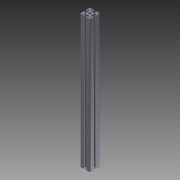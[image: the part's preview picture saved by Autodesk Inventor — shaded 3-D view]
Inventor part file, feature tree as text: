
AUTODESK INVENTOR PART (.ipt)
format: ipt  version: 2016 (Build 200138000, 138)  size: 215,552 bytes
history: native  units: mm
features: other x42, sketch x5, hole x4, extrude x1
ambient origin geometry x8: Origin, YZ Plane, XZ Plane, XY Plane, X Axis, Y Axis, Z Axis, Center Point
bodies: Solid1 (feature_tree)
feature tree (52):
  extrude  "Extrusion1"  [1 undecoded]
  hole  "Drilling 1"  [1 undecoded]
  hole  "Drilling 2"  [1 undecoded]
  hole  "Drilling 3"  [1 undecoded]
  hole  "Drilling 4"  [1 undecoded]
  other  "side_4d_XY"
  other  "side_4d_YZ"
  other  "side_4d_ZX"
  other  "side_4d_X"
  other  "side_4d_Y"
  other  "side_4d_Z"
  other  "side_4d_Center"
  other  "side_1a_XY"
  other  "side_1a_YZ"
  other  "side_1a_ZX"
  other  "side_1a_X"
  other  "side_1a_Y"
  other  "side_1a_Z"
  other  "side_1a_Center"
  other  "side_2b_XY"
  other  "side_2b_YZ"
  other  "side_2b_ZX"
  other  "side_2b_X"
  other  "side_2b_Y"
  other  "side_2b_Z"
  other  "side_2b_Center"
  other  "side_3c_XY"
  other  "side_3c_YZ"
  other  "side_3c_ZX"
  other  "side_3c_X"
  other  "side_3c_Y"
  other  "side_3c_Z"
  other  "side_3c_Center"
  other  "end_XY"
  other  "end_YZ"
  other  "end_ZX"
  other  "end_X"
  other  "end_Y"
  other  "end_Z"
  other  "end_Center"
  other  "start_XY"
  other  "start_YZ"
  other  "start_ZX"
  other  "start_X"
  other  "start_Y"
  other  "start_Z"
  other  "start_Center"
  sketch  "Skizze_1"  dims[d0=550.0mm d1=0.0mm]
  sketch  "Sketch2"  dims[d2=5.0mm d3=6.0mm d4=4.0mm d5=2.0mm d6=90.0deg d7=6000.0mm d8=0.0mm]
  sketch  "Sketch3"  dims[d9=5.0mm d10=6.0mm d11=4.0mm d12=2.0mm d13=90.0deg d14=6000.0mm d15=0.0mm]
  sketch  "Sketch4"  dims[d16=5.0mm d17=6.0mm d18=4.0mm d19=2.0mm d20=90.0deg d21=6000.0mm d22=0.0mm]
  sketch  "Sketch5"  dims[d23=5.0mm d24=6.0mm d25=4.0mm d26=2.0mm d27=90.0deg d28=6000.0mm d29=0.0mm]
note: 5 required parameter values undecoded (feature->parameter linkage not recoverable at this tier; creation-order binding heuristic only, values carry confidence <= 0.55)
